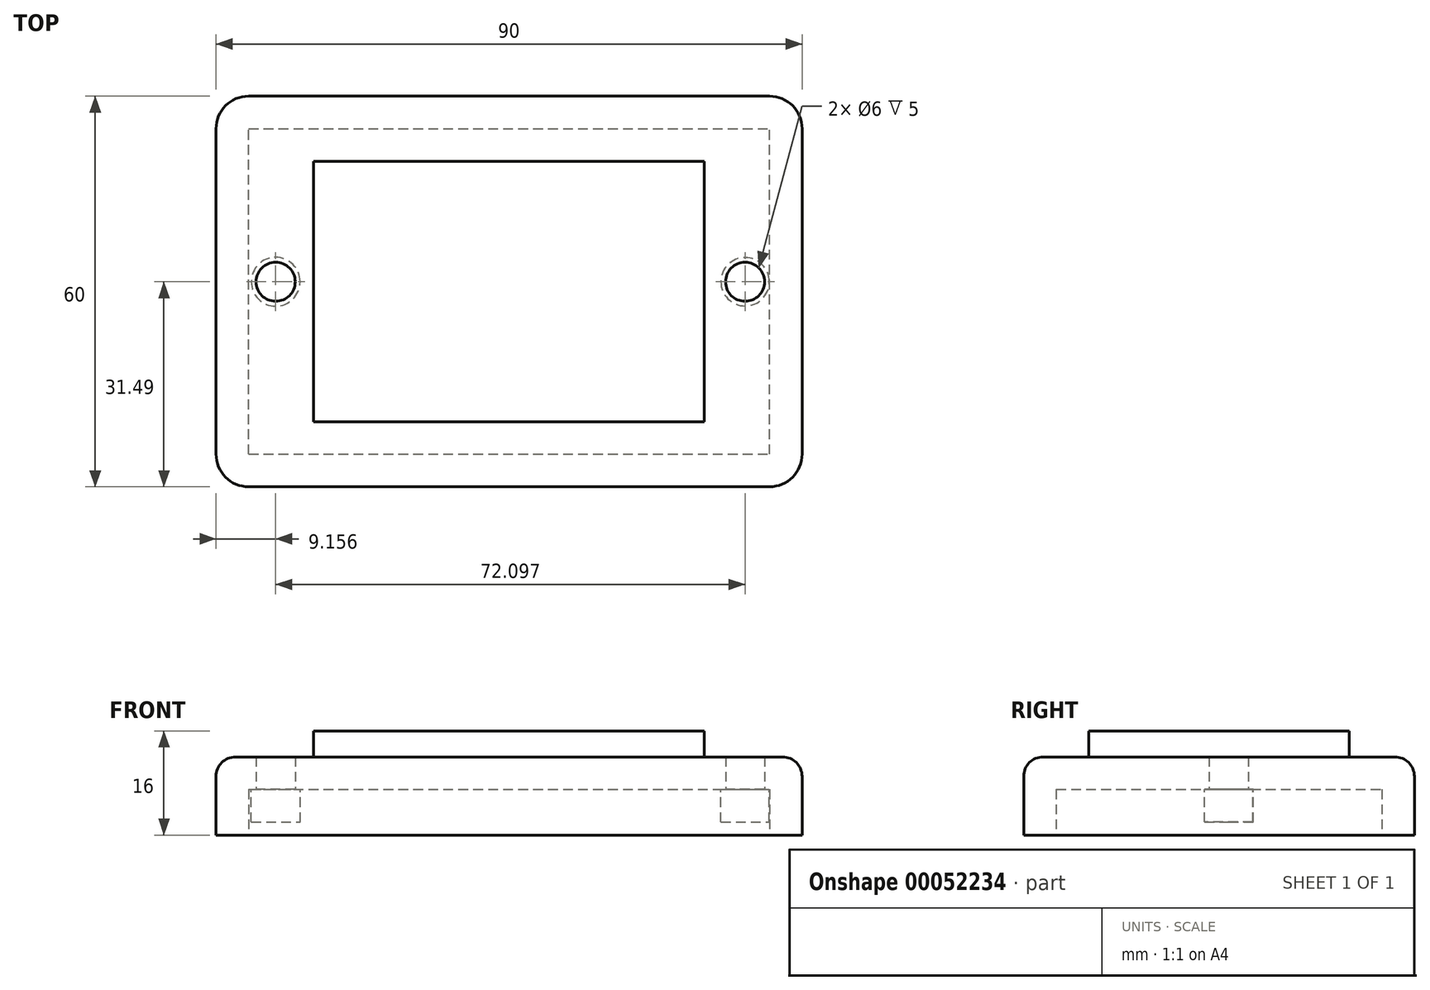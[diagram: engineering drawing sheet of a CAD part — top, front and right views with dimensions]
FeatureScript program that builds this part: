
annotation { "Feature Type Name" : "Feature", "Feature Type Description" : "" }
export const myFeature = defineFeature(function(context is Context, id is Id, definition is map)
    precondition{}
    {
        {
            var Q0;
            Q0=qCreatedBy(makeId("Top.planeOp"),FACE);
            var sketch = newSketch(context, id + "F0", { "sketchPlane" : qUnion([Q0])});
            skLineSegment(sketch, "E0.bottom", {"start": v(-45, 28.51) * mm, "end": v(45, 28.51) * mm});
            skLineSegment(sketch, "E0.top", {"start": v(-45, -31.49) * mm, "end": v(45, -31.49) * mm});
            skLineSegment(sketch, "E0.left", {"start": v(-45, 28.51) * mm, "end": v(-45, -31.49) * mm});
            skLineSegment(sketch, "E0.right", {"start": v(45, 28.51) * mm, "end": v(45, -31.49) * mm});
            skSolve(sketch);
        }
        {
            var Q0;
            Q0 = qSketchRegion(id + "F0", true);
            extrude(context, id + "F1", {"entities" : qUnion([Q0]), "depth" : 5 * mm});
        }
        {
            var Q0;
            Q0=makeQuery(id+"F1.opExtrude","CAP_FACE",FACE,{"disambiguationData":[OSD([sQuery(id+"F0.wireOp",EDGE,"E0.bottom"),sQuery(id+"F0.wireOp",EDGE,"E0.top"),sQuery(id+"F0.wireOp",EDGE,"E0.left"),sQuery(id+"F0.wireOp",EDGE,"E0.right")])],"isStart":false});
            var sketch = newSketch(context, id + "F2", { "sketchPlane" : qUnion([Q0])});
            skLineSegment(sketch, "E1.bottom", {"start": v(-30, 18.51) * mm, "end": v(30, 18.51) * mm});
            skLineSegment(sketch, "E1.top", {"start": v(-30, -21.49) * mm, "end": v(30, -21.49) * mm});
            skLineSegment(sketch, "E1.left", {"start": v(-30, 18.51) * mm, "end": v(-30, -21.49) * mm});
            skLineSegment(sketch, "E1.right", {"start": v(30, 18.51) * mm, "end": v(30, -21.49) * mm});
            skSolve(sketch);
        }
        {
            var Q0;
            Q0 = qSketchRegion(id + "F2", true);
            extrude(context, id + "F3", {"entities" : qUnion([Q0]), "operationType" : NewBodyOperationType.ADD, "depth" : 4 * mm});
        }
        {
            var Q0;
            Q0=makeQuery(id+"F1.opExtrude","SWEPT_EDGE",EDGE,{"disambiguationData":[OSD([sQuery(id+"F0.wireOp",EDGE,"E0.bottom"),sQuery(id+"F0.wireOp",EDGE,"E0.left")])]});
            var Q1;
            Q1=makeQuery(id+"F1.opExtrude","SWEPT_EDGE",EDGE,{"disambiguationData":[OSD([sQuery(id+"F0.wireOp",EDGE,"E0.bottom"),sQuery(id+"F0.wireOp",EDGE,"E0.right")])]});
            var Q2;
            Q2=makeQuery(id+"F1.opExtrude","SWEPT_EDGE",EDGE,{"disambiguationData":[OSD([sQuery(id+"F0.wireOp",EDGE,"E0.top"),sQuery(id+"F0.wireOp",EDGE,"E0.right")])]});
            var Q3;
            Q3=makeQuery(id+"F1.opExtrude","SWEPT_EDGE",EDGE,{"disambiguationData":[OSD([sQuery(id+"F0.wireOp",EDGE,"E0.top"),sQuery(id+"F0.wireOp",EDGE,"E0.left")])]});
            fillet(context, id + "F4", {"entities" : qUnion([Q0, Q1, Q2, Q3]), "radius" : 5 * mm, "tangentPropagation" : true, "allowEdgeOverflow" : false});
        }
        {
            var Q0;
            Q0=makeQuery(id+"F1.opExtrude","CAP_EDGE",EDGE,{"disambiguationData":[OSD([sQuery(id+"F0.wireOp",EDGE,"E0.bottom")])],"isStart":false});
            fillet(context, id + "F5", {"entities" : qUnion([Q0]), "radius" : 3 * mm, "tangentPropagation" : true, "allowEdgeOverflow" : false});
        }
        {
            var Q0;
            Q0=makeQuery(id+"F1.opExtrude","CAP_FACE",FACE,{"disambiguationData":[OSD([sQuery(id+"F0.wireOp",EDGE,"E0.bottom"),sQuery(id+"F0.wireOp",EDGE,"E0.top"),sQuery(id+"F0.wireOp",EDGE,"E0.left"),sQuery(id+"F0.wireOp",EDGE,"E0.right")])],"isStart":false});
            var sketch = newSketch(context, id + "F6", { "sketchPlane" : qUnion([Q0])});
            skCircle(sketch, "E2", {"center": v(-36, 0) * mm, "radius": 3 * mm});
            skCircle(sketch, "E3", {"center": v(36, 0) * mm, "radius": 3 * mm});
            skSolve(sketch);
        }
        {
            var Q0;
            Q0=qCreatedBy(makeId("Top.planeOp"),FACE);
            var sketch = newSketch(context, id + "F7", { "sketchPlane" : qUnion([Q0])});
            skCircle(sketch, "E4", {"center": v(-35.84, 0) * mm, "radius": 3 * mm});
            skCircle(sketch, "E5", {"center": v(36.25, 0) * mm, "radius": 3 * mm});
            skSolve(sketch);
        }
        {
            var Q0;
            Q0=makeQuery(id+"F7.imprint","IMPRINT",FACE,{"disambiguationData":[TD([[makeQuery(id+"F7.imprint","IMPRINT",EDGE,{"derivedFrom":sQuery(id+"F7.wireOp",EDGE,"E4")}),1.0]])]});
            var Q1;
            Q1=makeQuery(id+"F7.imprint","IMPRINT",FACE,{"disambiguationData":[TD([[makeQuery(id+"F7.imprint","IMPRINT",EDGE,{"derivedFrom":sQuery(id+"F7.wireOp",EDGE,"E5")}),1.0]])]});
            extrude(context, id + "F8", {"entities" : qUnion([Q0, Q1]), "operationType" : NewBodyOperationType.REMOVE, "depth" : 10 * mm});
        }
        {
            var Q0;
            Q0=makeQuery(id+"F1.opExtrude","CAP_FACE",FACE,{"disambiguationData":[OSD([sQuery(id+"F0.wireOp",EDGE,"E0.bottom"),sQuery(id+"F0.wireOp",EDGE,"E0.top"),sQuery(id+"F0.wireOp",EDGE,"E0.left"),sQuery(id+"F0.wireOp",EDGE,"E0.right")])],"isStart":true});
            var sketch = newSketch(context, id + "F9", { "sketchPlane" : qUnion([Q0])});
            skSolve(sketch);
        }
        {
            var Q0;
            Q0 = qSketchRegion(id + "F9", true);
            var Q1;
            {var subQ3=sQuery(id+"F0.wireOp",EDGE,"E0.bottom");Q1=makeQuery(id+"F9.imprint","IMPRINT",FACE,{"disambiguationData":[TD([[makeQuery(id+"F9.imprint","IMPRINT",EDGE,{"derivedFrom":makeQuery(id+"F1.opExtrude","CAP_EDGE",EDGE,{"disambiguationData":[OSD([subQ3])],"isStart":true})}),1.0]])]});}
            extrude(context, id + "F10", {"entities" : qUnion([Q0, Q1]), "operationType" : NewBodyOperationType.ADD, "depth" : 7 * mm});
        }
        {
            var Q0;
            Q0=makeQuery(id+"F10.opExtrude","CAP_FACE",FACE,{"disambiguationData":[OSD([sQuery(id+"F0.wireOp",EDGE,"E0.bottom"),sQuery(id+"F0.wireOp",EDGE,"E0.top"),sQuery(id+"F0.wireOp",EDGE,"E0.left"),sQuery(id+"F0.wireOp",EDGE,"E0.right"),sQuery(id+"F7.wireOp",EDGE,"E4"),sQuery(id+"F7.wireOp",EDGE,"E5")])],"isStart":false});
            var sketch = newSketch(context, id + "F11", { "sketchPlane" : qUnion([Q0])});
            skLineSegment(sketch, "E6.bottom", {"start": v(-40, 26.49) * mm, "end": v(40, 26.49) * mm});
            skLineSegment(sketch, "E6.top", {"start": v(-40, -23.51) * mm, "end": v(40, -23.51) * mm});
            skLineSegment(sketch, "E6.left", {"start": v(-40, 26.49) * mm, "end": v(-40, -23.51) * mm});
            skLineSegment(sketch, "E6.right", {"start": v(40, 26.49) * mm, "end": v(40, -23.51) * mm});
            skSolve(sketch);
        }
        {
            var Q0;
            Q0=makeQuery(id+"F11.imprint","IMPRINT",FACE,{"disambiguationData":[TD([[makeQuery(id+"F11.imprint","IMPRINT",EDGE,{"derivedFrom":sQuery(id+"F11.wireOp",EDGE,"E6.bottom")}),-1.0]])]});
            extrude(context, id + "F12", {"entities" : qUnion([Q0]), "operationType" : NewBodyOperationType.REMOVE, "oppositeDirection" : true, "depth" : 7 * mm});
        }
        {
            var Q0;
            Q0=makeQuery(id+"F12.boolean.opBoolean","COPY",FACE,{"derivedFrom":makeQuery(id+"F12.opExtrude","CAP_FACE",FACE,{"disambiguationData":[OSD([sQuery(id+"F7.wireOp",EDGE,"E4"),sQuery(id+"F7.wireOp",EDGE,"E5"),sQuery(id+"F11.wireOp",EDGE,"E6.bottom"),sQuery(id+"F11.wireOp",EDGE,"E6.top"),sQuery(id+"F11.wireOp",EDGE,"E6.left"),sQuery(id+"F11.wireOp",EDGE,"E6.right")])],"isStart":false})});
            var sketch = newSketch(context, id + "F13", { "sketchPlane" : qUnion([Q0])});
            skCircle(sketch, "E7", {"center": v(-35.84, 0) * mm, "radius": 3.75 * mm});
            skSolve(sketch);
        }
        {
            var Q0;
            Q0 = qSketchRegion(id + "F13", true);
            extrude(context, id + "F14", {"entities" : qUnion([Q0]), "operationType" : NewBodyOperationType.ADD, "depth" : 5 * mm});
        }
        {
            var Q0;
            Q0=makeQuery(id+"F12.boolean.opBoolean","COPY",FACE,{"derivedFrom":makeQuery(id+"F12.opExtrude","CAP_FACE",FACE,{"disambiguationData":[OSD([sQuery(id+"F7.wireOp",EDGE,"E4"),sQuery(id+"F7.wireOp",EDGE,"E5"),sQuery(id+"F11.wireOp",EDGE,"E6.bottom"),sQuery(id+"F11.wireOp",EDGE,"E6.top"),sQuery(id+"F11.wireOp",EDGE,"E6.left"),sQuery(id+"F11.wireOp",EDGE,"E6.right")])],"isStart":false})});
            var sketch = newSketch(context, id + "F15", { "sketchPlane" : qUnion([Q0])});
            skCircle(sketch, "E8", {"center": v(36.25, 0) * mm, "radius": 3.72 * mm});
            skSolve(sketch);
        }
        {
            var Q0;
            Q0 = qSketchRegion(id + "F15", true);
            extrude(context, id + "F16", {"entities" : qUnion([Q0]), "operationType" : NewBodyOperationType.ADD, "depth" : 5 * mm});
        }
    });
